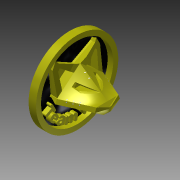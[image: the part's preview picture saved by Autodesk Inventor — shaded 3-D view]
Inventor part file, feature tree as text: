
AUTODESK INVENTOR PART (.ipt)
format: ipt  version: 2014 (Build 180170000, 170)  size: 1,433,600 bytes
history: native  units: in
note: dims shown in document units (in); Inventor stores cm internally (conversion verified against a paired STEP export)
features: sketch x23, extrude x16, plane x9, projected_geometry x8, loft x4, other x4, fillet x2, mirror x1, chamfer x1
ambient origin geometry x8: Origin, YZ Plane, XZ Plane, XY Plane, X Axis, Y Axis, Z Axis, Center Point
bodies: Solid1 (feature_tree)
feature tree (68):
  sketch  "Sketch1"  dims[d0=0.7559in d1=0.7559in]
  plane  "Work Plane1"
  loft  "Main Body"
  extrude  "Right Eye"  Depth=0.2in
  plane  "Work Plane4"
  loft  "Main Nose"
  plane  "Work Plane5"
  loft  "Back of Head"
  loft  "Main Ear - Right"
  extrude  "Inside of Ear - Right"  TaperAngle=0.0deg  [1 undecoded]
  plane  "Work Plane6"
  extrude  "Top and TopSide Rivets - Long"  Depth=1.0in
  extrude  "Top Most Rivet -  Cut Down"  Depth=1.0651in
  extrude  "Top Lower Rivet - Cut Down"  Depth=0.962in
  plane  "Work Plane7"
  extrude  "Side Rivets"  Depth=0.075in
  plane  "Work Plane8"
  other  "Work Axis1"
  plane  "Work Plane9"
  extrude  "Ear Shaping - Right"  Depth=0.06in
  mirror  "Eye, Ear and Rivet Mirro"
  extrude  "Fill Back (Make it a flat Print)"  Depth=0.05in
  plane  "Work Plane10"
  extrude  "Fill Back 2"  Depth=0.0625in
  plane  "Work Plane11"
  extrude  "Cut Back 1 (Adjust Angle)"  Depth=0.075in
  extrude  "Cut Back 2"  TaperAngle=0.0deg  [1 undecoded]
  extrude  "Round Back"  Depth=0.2in
  extrude  "Lip"  TaperAngle=0.0deg  [1 undecoded]
  other  "Team Text"
  extrude  "Remove Area for Ears"  Depth=0.01in
  extrude  "Remove Area for Nose"  Depth=0.0344in
  chamfer  "Chamfer Eyes"  Distance=0.05in
  fillet  "Fill Bridge of Nose"  Radius=0.05in
  extrude  "Extrusion18"  Depth=0.02in
  fillet  "Fillet3"  Radius=0.05in
  sketch  "Sketch2"  dims[d2=0.9963in d3=0.2in]
  sketch  "Sketch3"  dims[d4=0.5in d6=0.08in]
  sketch  "Sketch4"  dims[d7=0.55in d8=150.0deg]
  other  "Edges1"
  sketch  "Sketch5"  dims[d9=150.0deg d14=0.33in]
  projected_geometry  "Projected Loop1"
  other  "Edges2"
  sketch  "Sketch6"  dims[d15=0.66in d18=0.0in d19=90.0deg]
  sketch  "Sketch7"  dims[d20=0.0in d21=90.0deg d22=1.0in]
  sketch  "Sketch8"  dims[d26=1.0651in d28=1.0651in]
  sketch  "Sketch9"  dims[d29=0.0in d30=0.962in]
  sketch  "Sketch10"  dims[d31=0.962in d32=0.075in]
  sketch  "Sketch11"  dims[d33=0.15in d34=0.06in]
  sketch  "Sketch12"  dims[d35=0.1in d36=0.05in]
  sketch  "Sketch13"  dims[d37=0.45in d38=0.0in d39=0.0625in]
  projected_geometry  "Projected Loop2"
  projected_geometry  "Projected Loop3"
  sketch  "Sketch14"  dims[d40=0.01in d41=0.075in]
  projected_geometry  "Projected Loop4"
  sketch  "Sketch15"  dims[d42=0.01in d43=0.0in d44=90.0deg]
  sketch  "Sketch16"  dims[d45=0.0in d46=90.0deg d47=0.2in]
  sketch  "Sketch17"  dims[d48=0.07in d49=0.0in d50=90.0deg]
  sketch  "Sketch18"  dims[d51=0.0in d52=90.0deg d53=0.01in]
  sketch  "Sketch19"  dims[d54=0.01in d55=0.0344in]
  sketch  "Sketch20"  dims[d56=150.0deg]
  sketch  "Sketch23"  dims[d57=60.0deg]
  projected_geometry  "Projected Loop6"
  sketch  "Sketch24"  dims[d58=150.0deg]
  sketch  "Sketch25"  dims[d59=0.7in d60=0.05in d61=0.05in d62=0.05in d63=0.05in d64=0.05in d65=0.01in d66=0.0in d67=90.0deg d68=0.0in d69=90.0deg d70=0.1in d71=0.4in d72=0.15in d73=0.05in d74=0.0in d75=0.02in d77=0.15in d78=0.02in d79=0.1in d80=0.1in d81=0.1in d82=0.02in d83=0.15in d84=0.05in d85=0.0in d86=0.045in d87=0.0in d88=0.025in d89=0.0in d90=0.02in d91=0.02in d92=0.005in d93=0.0in d94=90.0deg d95=0.4466in d96=1.0in d97=0.0in d98=1.0in d99=0.0in d100=0.6528in d101=0.0in d102=0.0in d103=1.0in d104=0.0in d106=90.0deg d107=1.0in d108=0.0in d109=1.65in d110=0.1in d111=0.075in d112=0.0in d113=0.1in d114=0.075in d115=0.0in d116=0.05in d117=0.0in d123=0.1in d124=0.0in d125=0.05in d126=0.0in d130=0.02in d131=0.125in d132=45.0deg d133=0.02in d135=0.0375in d136=0.0in d137=0.02in]
  projected_geometry  "Projected Loop7"
  projected_geometry  "Projected Loop8"
  projected_geometry  "Projected Loop9"
note: 3 required parameter values undecoded (feature->parameter linkage not recoverable at this tier; creation-order binding heuristic only, values carry confidence <= 0.55)
